# Revit family: Tables-Meeting-Teknion-BC_CHP_Height_Adjustable_Conference_Table_Panel_Bases-R2019
name_source: partatom
category: Furniture
units: mm (PartAtom-declared; Revit-internal decimal feet)

## family parameters
Always vertical = Yes
Cut with Voids When Loaded = No
OmniClass Number = 23.40.20.00
OmniClass Title = General Furniture and Specialties
Room Calculation Point = No
Shared = Yes
Work Plane-Based = No

## types (7) — shared parameters
Assembly Code = E2020200
Manufacturer = Teknion
Manufacturer Fax = 416.661.4586
Part Number = BC_CHP
Product Documentation Link = https://www.teknion.com
Product Line = Expansion Casegoods
Product Page URL = https://www.teknion.com
Series = Expansion Casegoods
Sustainability Data = https://www.teknion.com
URL = www.teknion.com
Unit Weight URL = http://www.teknion.com
Warranty = http://www.teknion.com

## per-type parameters (varying)
| type | Depth | Description | Frame Depth | Model | Worksurface Thickness |
| 1 3/16" Worksurface Thickness, Standard Range, 60" Depth | 59.7 " | Height-Adjustable Conference Table - Panel Base, 1 3/16" Worksurface Thickness, Standard Range - 28" to 43", 60" Depth | 40.819 " | BCMCHPS60_____ | 1.189 " |
| 1 3/16" Worksurface Thickness, Standard Range, 54" Depth | 53.73 " | Height-Adjustable Conference Table - Panel Base, 1 3/16" Worksurface Thickness, Standard Range - 28" to 43", 54" Depth | 40.819 " | BCMCHPS54_____ | 1.189 " |
| 1 3/16" Worksurface Thickness, Standard Range, 48" Depth | 47.76 " | Height-Adjustable Conference Table - Panel Base, 1 3/16" Worksurface Thickness, Standard Range - 28" to 43", 48" Depth | 34.819 " | BCMCHPS48_____ | 1.189 " |
| 1 3/16" Worksurface Thickness, Standard Range, 42" Depth | 41.79 " | Height-Adjustable Conference Table - Panel Base, 1 3/16" Worksurface Thickness, Standard Range - 28" to 43", 42" Depth | 34.819 " | BCMCHPS42_____ | 1.189 " |
| 1 9/16" Worksurface Thickness, Standard Range, 42" Depth | 41.79 " | Height-Adjustable Conference Table - Panel Base, 1 9/16" Worksurface Thickness, Standard Range - 28" to 43", 42" Depth | 34.819 " | BCXCHPS42_____ | 1.555 " |
| 1 9/16" Worksurface Thickness, Standard Range, 48" Depth | 47.76 " | Height-Adjustable Conference Table - Panel Base, 1 9/16" Worksurface Thickness, Standard Range - 28" to 43", 48" Depth | 34.819 " | BCXCHPS48_____ | 1.555 " |
| 1 9/16" Worksurface Thickness, Standard Range, 54" Depth | 53.73 " | Height-Adjustable Conference Table - Panel Base, 1 9/16" Worksurface Thickness, Standard Range - 28" to 43", 54" Depth | 40.819 " | BCXCHPS54_____ | 1.555 " |

## geometry (parser evidence)
native form markers: Sweep x3
no freeform markers — native parametric forms only
